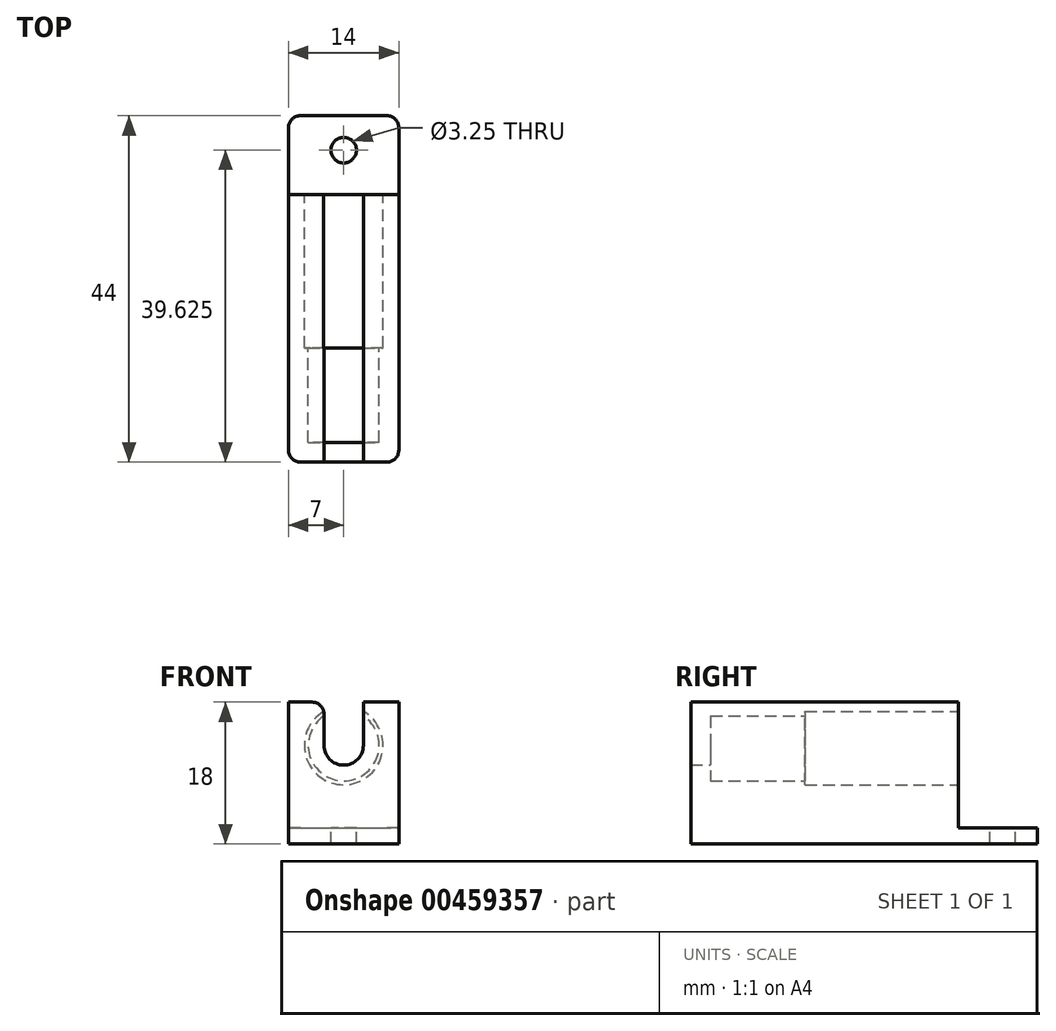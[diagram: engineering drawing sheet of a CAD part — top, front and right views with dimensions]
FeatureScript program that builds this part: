
annotation { "Feature Type Name" : "Feature", "Feature Type Description" : "" }
export const myFeature = defineFeature(function(context is Context, id is Id, definition is map)
    precondition{}
    {
        {
            var Q0;
            Q0=qCreatedBy(makeId("Top.planeOp"),FACE);
            var sketch = newSketch(context, id + "F0", { "sketchPlane" : qUnion([Q0])});
            skLineSegment(sketch, "E0.bottom", {"start": v(0, 0) * mm, "end": v(14, 0) * mm});
            skLineSegment(sketch, "E0.top", {"start": v(0, 44) * mm, "end": v(14, 44) * mm});
            skLineSegment(sketch, "E0.left", {"start": v(0, 0) * mm, "end": v(0, 44) * mm});
            skLineSegment(sketch, "E0.right", {"start": v(14, 0) * mm, "end": v(14, 44) * mm});
            skSolve(sketch);
        }
        {
            var Q0;
            Q0 = qSketchRegion(id + "F0", true);
            extrude(context, id + "F1", {"entities" : qUnion([Q0]), "depth" : 18 * mm});
        }
        {
            var Q0;
            Q0=makeQuery(id+"F1.opExtrude","CAP_FACE",FACE,{"disambiguationData":[OSD([sQuery(id+"F0.wireOp",EDGE,"E0.bottom"),sQuery(id+"F0.wireOp",EDGE,"E0.top"),sQuery(id+"F0.wireOp",EDGE,"E0.left"),sQuery(id+"F0.wireOp",EDGE,"E0.right")])],"isStart":false});
            var sketch = newSketch(context, id + "F2", { "sketchPlane" : qUnion([Q0])});
            skLineSegment(sketch, "E1.bottom", {"start": v(0, 44) * mm, "end": v(14, 44) * mm});
            skLineSegment(sketch, "E1.top", {"start": v(0, 34) * mm, "end": v(14, 34) * mm});
            skLineSegment(sketch, "E1.left", {"start": v(0, 44) * mm, "end": v(0, 34) * mm});
            skLineSegment(sketch, "E1.right", {"start": v(14, 44) * mm, "end": v(14, 34) * mm});
            skSolve(sketch);
        }
        {
            var Q0;
            Q0 = qSketchRegion(id + "F2", true);
            extrude(context, id + "F3", {"entities" : qUnion([Q0]), "operationType" : NewBodyOperationType.REMOVE, "oppositeDirection" : true, "depth" : 16 * mm});
        }
        {
            var Q0;
            Q0=makeQuery(id+"F3.boolean.opBoolean","COPY",FACE,{"derivedFrom":makeQuery(id+"F3.opExtrude","CAP_FACE",FACE,{"disambiguationData":[OSD([sQuery(id+"F2.wireOp",EDGE,"E1.bottom"),sQuery(id+"F2.wireOp",EDGE,"E1.top"),sQuery(id+"F2.wireOp",EDGE,"E1.left"),sQuery(id+"F2.wireOp",EDGE,"E1.right")])],"isStart":false})});
            var sketch = newSketch(context, id + "F4", { "sketchPlane" : qUnion([Q0])});
            skCircle(sketch, "E2", {"center": v(7, 39.62) * mm, "radius": 1.63 * mm});
            skLineSegment(sketch, "E3", {"start": v(7, 44) * mm, "end": v(7, 34) * mm, "construction": true});
            skSolve(sketch);
        }
        {
            var Q0;
            Q0 = qSketchRegion(id + "F4", true);
            extrude(context, id + "F5", {"entities" : qUnion([Q0]), "operationType" : NewBodyOperationType.REMOVE, "endBound" : BoundingType.UP_TO_NEXT, "oppositeDirection" : true, "depth" : 5 * mm});
        }
        {
            var Q0;
            Q0=makeQuery(id+"F3.boolean.opBoolean","COPY",FACE,{"derivedFrom":makeQuery(id+"F3.opExtrude","SWEPT_FACE",FACE,{"disambiguationData":[OSD([sQuery(id+"F2.wireOp",EDGE,"E1.top")])]})});
            var sketch = newSketch(context, id + "F6", { "sketchPlane" : qUnion([Q0])});
            skLineSegment(sketch, "E4", {"start": v(-7, 2) * mm, "end": v(-7, 7.5) * mm, "construction": true});
            skCircle(sketch, "E5", {"center": v(-7, 12.5) * mm, "radius": 5 * mm});
            skCircle(sketch, "E6", {"center": v(-7, 12.5) * mm, "radius": 2.5 * mm});
            skCircle(sketch, "E7", {"center": v(-7, 12.5) * mm, "radius": 4.5 * mm});
            skSolve(sketch);
        }
        {
            var Q0;
            Q0=makeQuery(id+"F6.imprint","IMPRINT",FACE,{"disambiguationData":[TD([[makeQuery(id+"F6.imprint","IMPRINT",EDGE,{"derivedFrom":sQuery(id+"F6.wireOp",EDGE,"E6")}),1.0]])]});
            var Q1;
            Q1=makeQuery(id+"F1.opExtrude","SWEPT_FACE",FACE,{"disambiguationData":[OSD([sQuery(id+"F0.wireOp",EDGE,"E0.bottom")])]});
            extrude(context, id + "F7", {"entities" : qUnion([Q0]), "operationType" : NewBodyOperationType.REMOVE, "endBound" : BoundingType.UP_TO_SURFACE, "oppositeDirection" : true, "endBoundEntityFace" : qUnion([Q1]), "depth" : 25 * mm});
        }
        {
            var Q0;
            Q0=makeQuery(id+"F6.imprint","IMPRINT",FACE,{"disambiguationData":[TD([[makeQuery(id+"F6.imprint","IMPRINT",EDGE,{"derivedFrom":sQuery(id+"F6.wireOp",EDGE,"E6")}),-1.0]])]});
            extrude(context, id + "F8", {"entities" : qUnion([Q0]), "operationType" : NewBodyOperationType.REMOVE, "oppositeDirection" : true, "depth" : 31.5 * mm});
        }
        {
            var Q0;
            Q0=makeQuery(id+"F6.imprint","IMPRINT",FACE,{"disambiguationData":[TD([[makeQuery(id+"F6.imprint","IMPRINT",EDGE,{"derivedFrom":sQuery(id+"F6.wireOp",EDGE,"E5")}),1.0]])]});
            extrude(context, id + "F9", {"entities" : qUnion([Q0]), "operationType" : NewBodyOperationType.REMOVE, "oppositeDirection" : true, "depth" : 19.5 * mm});
        }
        {
            var Q0;
            Q0=makeQuery(id+"F6.imprint","IMPRINT",FACE,{"disambiguationData":[TD([[makeQuery(id+"F6.imprint","IMPRINT",EDGE,{"derivedFrom":sQuery(id+"F6.wireOp",EDGE,"E5")}),-1.0]])]});
            var sketch = newSketch(context, id + "F10", { "sketchPlane" : qUnion([Q0])});
            skLineSegment(sketch, "E8", {"start": v(-9.5, 18) * mm, "end": v(-9.5, 12.5) * mm});
            skLineSegment(sketch, "E9", {"start": v(-4.5, 18) * mm, "end": v(-4.5, 12.5) * mm});
            skLineSegment(sketch, "E10", {"start": v(-9.5, 18) * mm, "end": v(-4.5, 18) * mm});
            skCircle(sketch, "E11.0", {"center": v(-7, 12.5) * mm, "radius": 2.5 * mm});
            skSolve(sketch);
        }
        {
            var Q0;
            {var subQ0=sQuery(id+"F10.wireOp",EDGE,"E11.0");var subQ1=sQuery(id+"F10.wireOp",EDGE,"E8");var subQ2=makeQuery(id+"F10.imprint","INTERSECT",VERTEX,{"derivedFrom":[subQ1,subQ0]});Q0=makeQuery(id+"F10.imprint","IMPRINT",FACE,{"disambiguationData":[TD([[makeQuery(id+"F10.imprint","IMPRINT",EDGE,{"disambiguationData":[TD([[subQ2,1.0]])],"derivedFrom":subQ1}),1.0]])]});}
            var Q1;
            {var subQ0=sQuery(id+"F10.wireOp",EDGE,"E10");Q1=makeQuery(id+"F10.imprint","IMPRINT",FACE,{"disambiguationData":[TD([[makeQuery(id+"F10.imprint","IMPRINT",EDGE,{"derivedFrom":subQ0}),1.0]])]});}
            var Q2;
            Q2=makeQuery(id+"F1.opExtrude","SWEPT_FACE",FACE,{"disambiguationData":[OSD([sQuery(id+"F0.wireOp",EDGE,"E0.bottom")])]});
            extrude(context, id + "F11", {"entities" : qUnion([Q0, Q1]), "operationType" : NewBodyOperationType.REMOVE, "endBound" : BoundingType.UP_TO_SURFACE, "oppositeDirection" : true, "endBoundEntityFace" : qUnion([Q2]), "depth" : 25 * mm});
        }
        {
            var Q0;
            Q0=makeQuery(id+"F1.opExtrude","SWEPT_EDGE",EDGE,{"disambiguationData":[OSD([sQuery(id+"F0.wireOp",EDGE,"E0.top"),sQuery(id+"F0.wireOp",EDGE,"E0.left")])]});
            var Q1;
            Q1=makeQuery(id+"F1.opExtrude","SWEPT_EDGE",EDGE,{"disambiguationData":[OSD([sQuery(id+"F0.wireOp",EDGE,"E0.top"),sQuery(id+"F0.wireOp",EDGE,"E0.right")])]});
            var Q2;
            Q2=makeQuery(id+"F11.boolean.opBoolean","COPY",EDGE,{"derivedFrom":makeQuery(id+"F11.opExtrude","SWEPT_EDGE",EDGE,{"disambiguationData":[OSD([sQuery(id+"F2.wireOp",EDGE,"E1.top"),sQuery(id+"F10.wireOp",EDGE,"E9"),sQuery(id+"F10.wireOp",EDGE,"E10")])]})});
            var Q3;
            Q3=makeQuery(id+"F11.boolean.opBoolean","COPY",EDGE,{"derivedFrom":makeQuery(id+"F11.opExtrude","SWEPT_EDGE",EDGE,{"disambiguationData":[OSD([sQuery(id+"F2.wireOp",EDGE,"E1.top"),sQuery(id+"F10.wireOp",EDGE,"E8"),sQuery(id+"F10.wireOp",EDGE,"E10")])]})});
            var Q4;
            Q4=makeQuery(id+"F1.opExtrude","SWEPT_EDGE",EDGE,{"disambiguationData":[OSD([sQuery(id+"F0.wireOp",EDGE,"E0.bottom"),sQuery(id+"F0.wireOp",EDGE,"E0.right")])]});
            var Q5;
            Q5=makeQuery(id+"F1.opExtrude","SWEPT_EDGE",EDGE,{"disambiguationData":[OSD([sQuery(id+"F0.wireOp",EDGE,"E0.bottom"),sQuery(id+"F0.wireOp",EDGE,"E0.left")])]});
            var Q6;
            Q6=makeQuery(id+"F3.boolean.opBoolean","COPY",EDGE,{"derivedFrom":makeQuery(id+"F3.opExtrude","SWEPT_EDGE",EDGE,{"disambiguationData":[OSD([sQuery(id+"F0.wireOp",EDGE,"E0.left"),sQuery(id+"F2.wireOp",EDGE,"E1.top"),sQuery(id+"F2.wireOp",EDGE,"E1.left")])]})});
            var Q7;
            Q7=makeQuery(id+"F3.boolean.opBoolean","COPY",EDGE,{"derivedFrom":makeQuery(id+"F3.opExtrude","SWEPT_EDGE",EDGE,{"disambiguationData":[OSD([sQuery(id+"F0.wireOp",EDGE,"E0.right"),sQuery(id+"F2.wireOp",EDGE,"E1.top"),sQuery(id+"F2.wireOp",EDGE,"E1.right")])]})});
            fillet(context, id + "F12", {"entities" : qUnion([Q0, Q1, Q2, Q3, Q4, Q5, Q6, Q7]), "radius" : 1.5 * mm, "tangentPropagation" : true, "allowEdgeOverflow" : false});
        }
    });
